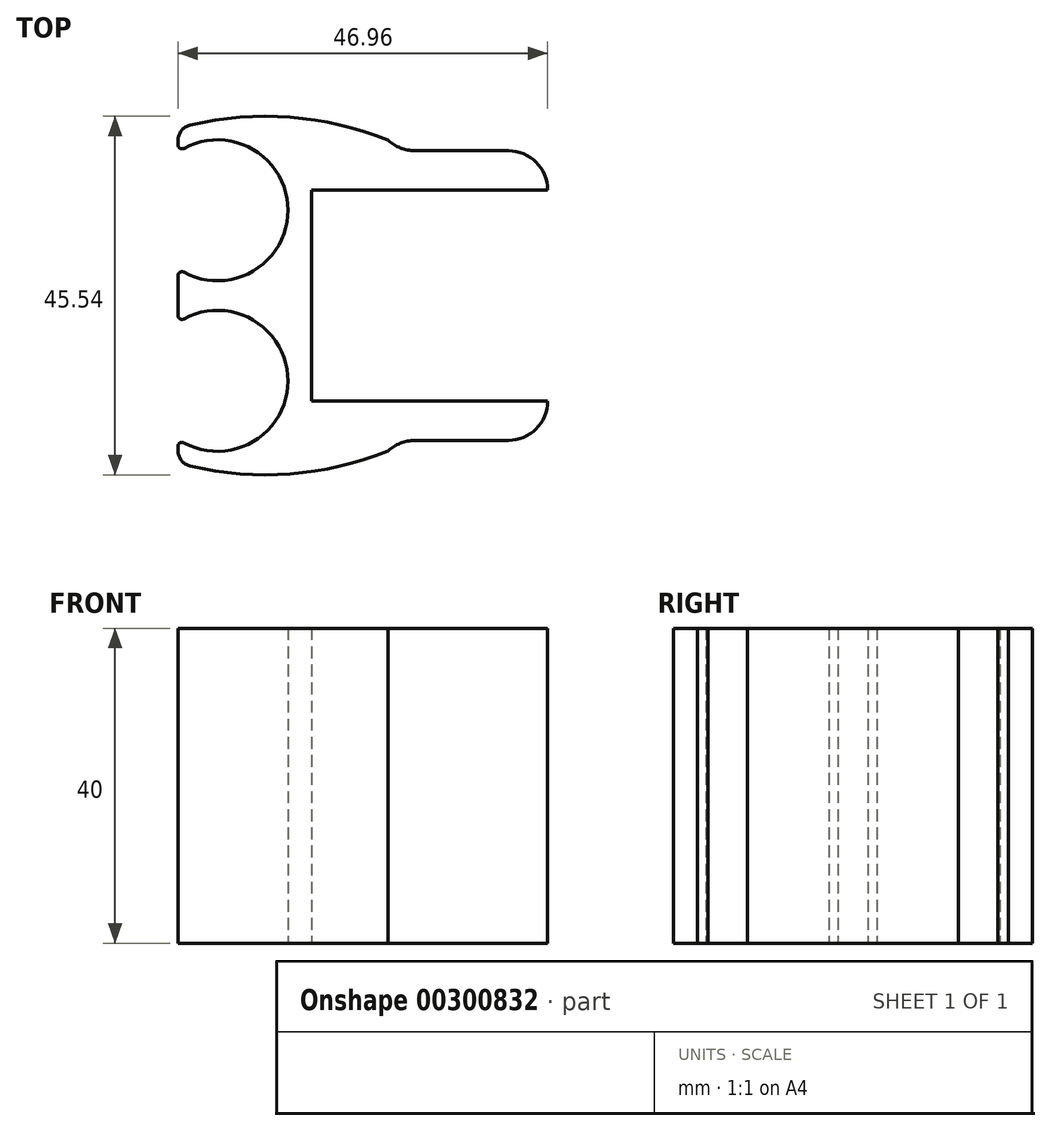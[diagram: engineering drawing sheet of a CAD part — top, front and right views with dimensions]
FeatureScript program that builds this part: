
annotation { "Feature Type Name" : "Feature", "Feature Type Description" : "" }
export const myFeature = defineFeature(function(context is Context, id is Id, definition is map)
    precondition{}
    {
        {
            var Q0;
            Q0=qCreatedBy(makeId("Top.planeOp"),FACE);
            var sketch = newSketch(context, id + "F0", { "sketchPlane" : qUnion([Q0])});
            skLineSegment(sketch, "E0.right", {"start": v(-17.27, 13.4) * mm, "end": v(-17.27, -13.4) * mm});
            skPoint(sketch, "E0.middle", {"position": v(0, 0) * mm});
            skLineSegment(sketch, "E1.top", {"start": v(-17.27, 13.4) * mm, "end": v(12.73, 13.4) * mm});
            skLineSegment(sketch, "E1.right", {"start": v(12.73, 13.4) * mm, "end": v(12.73, 13.4) * mm});
            skLineSegment(sketch, "E2.MirrorCS", {"start": v(-17.27, -13.4) * mm, "end": v(12.73, -13.4) * mm});
            skLineSegment(sketch, "E3.MirrorCS", {"start": v(12.73, -13.4) * mm, "end": v(12.73, -13.4) * mm});
            skPoint(sketch, "E4.orphan", {"position": v(-9.37, -3.54) * mm});
            skPoint(sketch, "E5.orphan", {"position": v(-9.37, 3.54) * mm});
            skLineSegment(sketch, "E6", {"start": v(7.73, 18.4) * mm, "end": v(-4.14, 18.4) * mm});
            skLineSegment(sketch, "E7.MirrorCS", {"start": v(7.73, -18.4) * mm, "end": v(-4.14, -18.4) * mm});
            skPoint(sketch, "E1.bottom.end.orphan", {"position": v(12.73, 58.28) * mm});
            skPoint(sketch, "E8.visualSharp", {"position": v(-6.11, -18.4) * mm});
            skArc(sketch, "E8.filletArc", {"start": v(-4.14, -18.4) * mm, "mid": v(-5.97, -18.75) * mm, "end": v(-7.55, -19.75) * mm});
            skPoint(sketch, "E9.visualSharp", {"position": v(-6.11, 18.4) * mm});
            skArc(sketch, "E9.filletArc", {"start": v(-7.55, 19.75) * mm, "mid": v(-5.97, 18.75) * mm, "end": v(-4.14, 18.4) * mm});
            skPoint(sketch, "E10.visualSharp", {"position": v(12.73, 18.4) * mm});
            skArc(sketch, "E10.filletArc", {"start": v(12.73, 13.4) * mm, "mid": v(11.26, 16.94) * mm, "end": v(7.73, 18.4) * mm});
            skPoint(sketch, "E11.visualSharp", {"position": v(12.73, -18.4) * mm});
            skArc(sketch, "E11.filletArc", {"start": v(7.73, -18.4) * mm, "mid": v(11.26, -16.94) * mm, "end": v(12.73, -13.4) * mm});
            skArc(sketch, "E12", {"start": v(-33.5, 2.97) * mm, "mid": v(-20.27, 10.83) * mm, "end": v(-33.5, 18.7) * mm});
            skPoint(sketch, "E13.end.orphan", {"position": v(-34.23, 0) * mm});
            skLineSegment(sketch, "E14", {"start": v(-34.23, 19.14) * mm, "end": v(-34.23, 19.7) * mm});
            skArc(sketch, "E15", {"start": v(-7.55, 19.75) * mm, "mid": v(-19.97, 22.65) * mm, "end": v(-32.7, 21.65) * mm});
            skPoint(sketch, "E16.visualSharp", {"position": v(-34.23, 21.25) * mm});
            skArc(sketch, "E16.filletArc", {"start": v(-32.7, 21.65) * mm, "mid": v(-33.8, 20.94) * mm, "end": v(-34.23, 19.7) * mm});
            skArc(sketch, "E17.MirrorCS", {"start": v(-33.5, -2.97) * mm, "mid": v(-20.27, -10.83) * mm, "end": v(-33.5, -18.7) * mm});
            skLineSegment(sketch, "E18.MirrorCS", {"start": v(-34.23, -19.14) * mm, "end": v(-34.23, -19.7) * mm});
            skArc(sketch, "E19.MirrorCS", {"start": v(-32.7, -21.65) * mm, "mid": v(-33.8, -20.94) * mm, "end": v(-34.23, -19.7) * mm});
            skArc(sketch, "E20.MirrorCS", {"start": v(-7.55, -19.75) * mm, "mid": v(-19.97, -22.65) * mm, "end": v(-32.7, -21.65) * mm});
            skLineSegment(sketch, "E21", {"start": v(-34.23, -2.53) * mm, "end": v(-34.23, 2.53) * mm});
            skPoint(sketch, "E22.visualSharp", {"position": v(-34.23, 18.25) * mm});
            skArc(sketch, "E22.filletArc", {"start": v(-34.23, 19.14) * mm, "mid": v(-33.99, 18.7) * mm, "end": v(-33.5, 18.7) * mm});
            skPoint(sketch, "E23.visualSharp", {"position": v(-34.23, 3.42) * mm});
            skArc(sketch, "E23.filletArc", {"start": v(-33.5, 2.97) * mm, "mid": v(-33.99, 2.96) * mm, "end": v(-34.23, 2.53) * mm});
            skPoint(sketch, "E24.visualSharp", {"position": v(-34.23, -3.42) * mm});
            skArc(sketch, "E24.filletArc", {"start": v(-34.23, -2.53) * mm, "mid": v(-33.99, -2.96) * mm, "end": v(-33.5, -2.97) * mm});
            skPoint(sketch, "E25.visualSharp", {"position": v(-34.23, -18.25) * mm});
            skArc(sketch, "E25.filletArc", {"start": v(-33.5, -18.7) * mm, "mid": v(-33.99, -18.7) * mm, "end": v(-34.23, -19.14) * mm});
            skSolve(sketch);
        }
        {
            var Q0;
            Q0=makeQuery(id+"F0.imprint","IMPRINT",FACE,{"disambiguationData":[TD([[makeQuery(id+"F0.imprint","IMPRINT",EDGE,{"derivedFrom":sQuery(id+"F0.wireOp",EDGE,"E0.right")}),-1.0]])]});
            extrude(context, id + "F1", {"entities" : qUnion([Q0]), "depth" : 40 * mm});
        }
    });
